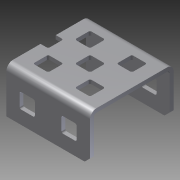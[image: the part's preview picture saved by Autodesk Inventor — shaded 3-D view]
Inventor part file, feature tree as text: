
AUTODESK INVENTOR PART (.ipt)
format: ipt  version: 2014 SP1 (Build 180222100, 222)  size: 332,288 bytes
history: native  units: in
note: dims shown in document units (in); Inventor stores cm internally (conversion verified against a paired STEP export)
features: other x1, imported_body x1, extrude x1, sketch x1
ambient origin geometry x8: Origin, YZ Plane, XZ Plane, XY Plane, X Axis, Y Axis, Z Axis, Center Point
bodies: Body1 (feature_tree)
feature tree (4):
  parser-record x1  (decoder bookkeeping rows leaked as tree rows — omitted from the tree; the rows remain in map.json)
  imported_body  "Base1"
  extrude  "Extrusion1"  Depth=1.0in TaperAngle=0.0deg
  sketch  "Sketch1"  dims[d0=1.5in d1=1.0in d2=0.0in]
